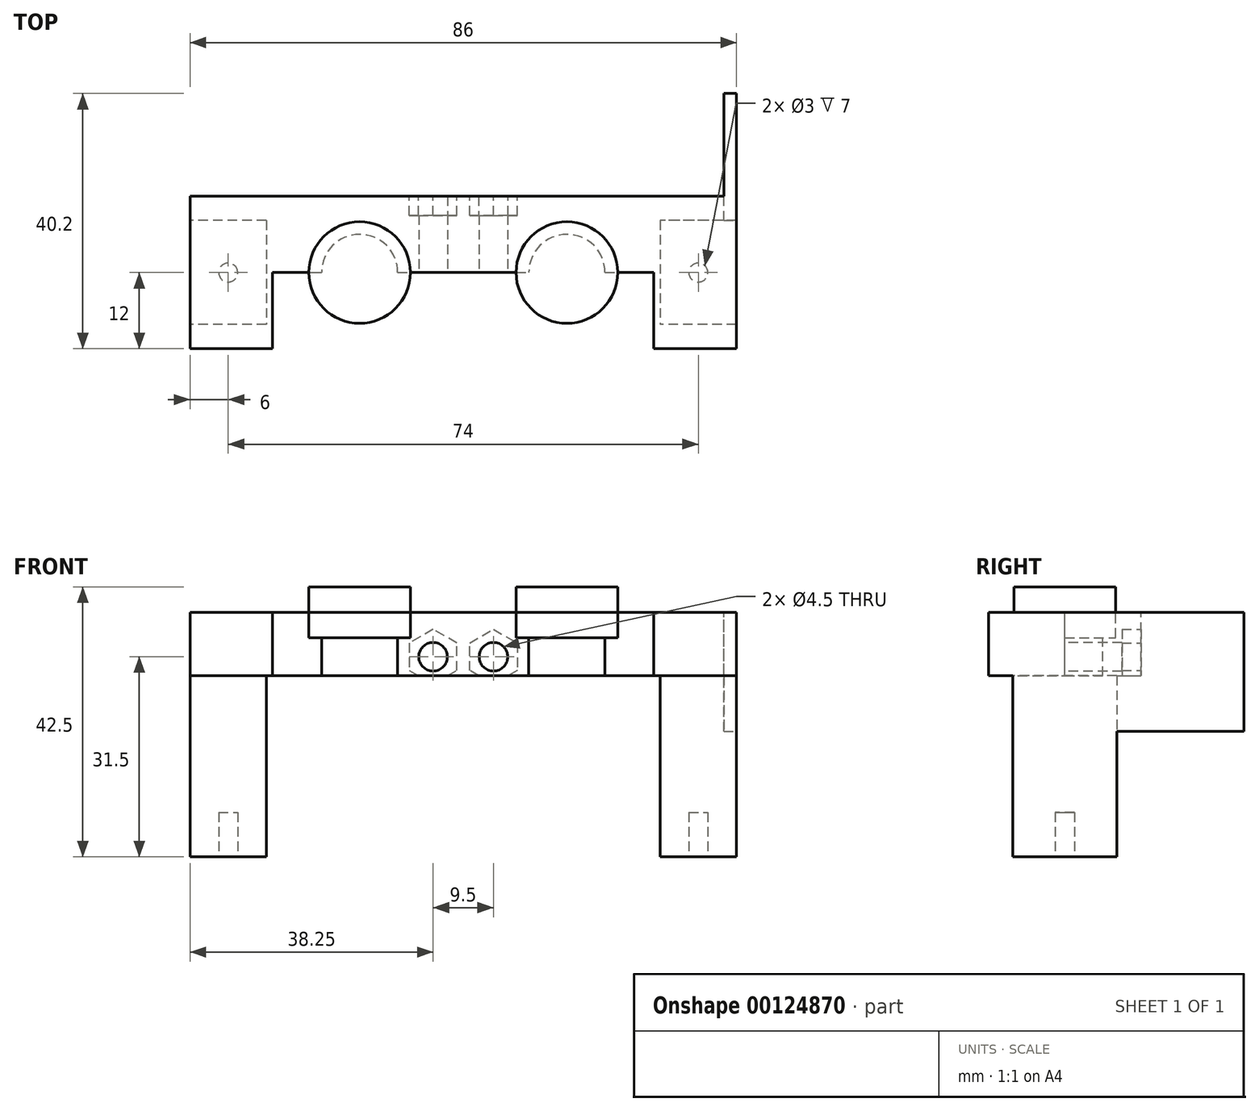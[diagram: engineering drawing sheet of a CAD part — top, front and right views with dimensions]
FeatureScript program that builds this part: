
annotation { "Feature Type Name" : "Feature", "Feature Type Description" : "" }
export const myFeature = defineFeature(function(context is Context, id is Id, definition is map)
    precondition{}
    {
        {
            var Q0;
            Q0=qCreatedBy(makeId("Top.planeOp"),FACE);
            var sketch = newSketch(context, id + "F0", { "sketchPlane" : qUnion([Q0])});
            skLineSegment(sketch, "E0.bottom", {"start": v(43, -44.5) * mm, "end": v(-43, -44.5) * mm});
            skLineSegment(sketch, "E0.top", {"start": v(43, 44.5) * mm, "end": v(-43, 44.5) * mm});
            skLineSegment(sketch, "E0.left", {"start": v(43, -44.5) * mm, "end": v(43, 44.5) * mm});
            skLineSegment(sketch, "E0.right", {"start": v(-43, -44.5) * mm, "end": v(-43, 44.5) * mm});
            skPoint(sketch, "E0.middle", {"position": v(0, 0) * mm});
            skLineSegment(sketch, "E1.bottom", {"start": v(-31, 25.5) * mm, "end": v(31, 25.5) * mm});
            skLineSegment(sketch, "E1.top", {"start": v(-31, -11.5) * mm, "end": v(31, -11.5) * mm});
            skLineSegment(sketch, "E1.left", {"start": v(-31, 25.5) * mm, "end": v(-31, -11.5) * mm});
            skLineSegment(sketch, "E1.right", {"start": v(31, 25.5) * mm, "end": v(31, -11.5) * mm});
            skLineSegment(sketch, "E2.bottom", {"start": v(43, 13.5) * mm, "end": v(31, 13.5) * mm});
            skLineSegment(sketch, "E2.top", {"start": v(43, -3) * mm, "end": v(31, -3) * mm});
            skLineSegment(sketch, "E2.left", {"start": v(43, 13.5) * mm, "end": v(43, -3) * mm});
            skLineSegment(sketch, "E2.right", {"start": v(-43, 13.5) * mm, "end": v(-43, -3) * mm});
            skLineSegment(sketch, "E3", {"start": v(-43, 5.25) * mm, "end": v(-31, 5.25) * mm, "construction": true});
            skLineSegment(sketch, "E4.trimOffspring", {"start": v(-31, 13.5) * mm, "end": v(-43, 13.5) * mm});
            skLineSegment(sketch, "E5.trimOffspring", {"start": v(-31, -3) * mm, "end": v(-43, -3) * mm});
            skLineSegment(sketch, "E6.trimOffspring", {"start": v(31, 5.25) * mm, "end": v(43, 5.25) * mm, "construction": true});
            skPoint(sketch, "E7", {"position": v(-37, 5.25) * mm});
            skPoint(sketch, "E8", {"position": v(37, 5.25) * mm});
            skCircle(sketch, "E9", {"center": v(37, 5.25) * mm, "radius": 1.6 * mm});
            skPoint(sketch, "E10", {"position": v(38.6, 5.25) * mm});
            skCircle(sketch, "E11.MirrorC", {"center": v(-37, 5.25) * mm, "radius": 1.6 * mm});
            skSolve(sketch);
        }
        {
            var Q0;
            Q0=qSketchRegion(id+"F0",true);
            extrude(context, id + "F1", {"entities" : qUnion([Q0]), "depth" : 17.5 * mm});
        }
        {
            var Q0;
            Q0=makeQuery(id+"F1.opExtrude","CAP_FACE",FACE,{"disambiguationData":[OSD([sQuery(id+"F0.wireOp",EDGE,"E0.bottom"),sQuery(id+"F0.wireOp",EDGE,"E0.top"),sQuery(id+"F0.wireOp",EDGE,"E0.left"),sQuery(id+"F0.wireOp",EDGE,"E0.right"),sQuery(id+"F0.wireOp",EDGE,"E1.bottom"),sQuery(id+"F0.wireOp",EDGE,"E1.top"),sQuery(id+"F0.wireOp",EDGE,"E1.left"),sQuery(id+"F0.wireOp",EDGE,"E1.right"),sQuery(id+"F0.wireOp",EDGE,"E2.left"),sQuery(id+"F0.wireOp",EDGE,"E2.right"),sQuery(id+"F0.wireOp",EDGE,"E9"),sQuery(id+"F0.wireOp",EDGE,"E11.MirrorC")])],"isStart":false});
            var sketch = newSketch(context, id + "F2", { "sketchPlane" : qUnion([Q0])});
            skLineSegment(sketch, "E12.bottom", {"start": v(43, -2.95) * mm, "end": v(31, -2.95) * mm});
            skLineSegment(sketch, "E12.top", {"start": v(43, 13.45) * mm, "end": v(31, 13.45) * mm});
            skLineSegment(sketch, "E12.left", {"start": v(43, -2.95) * mm, "end": v(43, 13.45) * mm});
            skLineSegment(sketch, "E12.right", {"start": v(-43, -2.95) * mm, "end": v(-43, 13.45) * mm});
            skPoint(sketch, "E13", {"position": v(37, 5.25) * mm});
            skLineSegment(sketch, "E14", {"start": v(43, 5.25) * mm, "end": v(31, 5.25) * mm, "construction": true});
            skLineSegment(sketch, "E15.0", {"start": v(31, 25.5) * mm, "end": v(31, -11.5) * mm});
            skLineSegment(sketch, "E15.1", {"start": v(-31, 25.5) * mm, "end": v(-31, -11.5) * mm});
            skLineSegment(sketch, "E16.trimOffspring", {"start": v(-31, -2.95) * mm, "end": v(-43, -2.95) * mm});
            skLineSegment(sketch, "E17.trimOffspring", {"start": v(-31, 13.45) * mm, "end": v(-43, 13.45) * mm});
            skLineSegment(sketch, "E18.trimOffspring", {"start": v(-31, 5.25) * mm, "end": v(-43, 5.25) * mm, "construction": true});
            skSolve(sketch);
        }
        {
            var Q0;
            Q0=qCreatedBy(makeId("Top.planeOp"),FACE);
            var sketch = newSketch(context, id + "F3", { "sketchPlane" : qUnion([Q0])});
            skCircle(sketch, "E19", {"center": v(16.32, 5.25) * mm, "radius": 11.2 * mm});
            skCircle(sketch, "E20.0", {"center": v(-37, 5.25) * mm, "radius": 1.6 * mm});
            skLineSegment(sketch, "E21", {"start": v(-37, 5.25) * mm, "end": v(47.23, 5.25) * mm, "construction": true});
            skCircle(sketch, "E22.MirrorC", {"center": v(-16.32, 5.25) * mm, "radius": 11.2 * mm});
            skSolve(sketch);
        }
        {
            var Q0;
            Q0=makeQuery(id+"F3.imprint","IMPRINT",FACE,{"disambiguationData":[TD([[makeQuery(id+"F3.imprint","IMPRINT",EDGE,{"derivedFrom":sQuery(id+"F3.wireOp",EDGE,"E19")}),1.0]])]});
            var Q1;
            Q1=makeQuery(id+"F3.imprint","IMPRINT",FACE,{"disambiguationData":[TD([[makeQuery(id+"F3.imprint","IMPRINT",EDGE,{"derivedFrom":sQuery(id+"F3.wireOp",EDGE,"E22.MirrorC")}),-1.0]])]});
            extrude(context, id + "F4", {"entities" : qUnion([Q0, Q1]), "depth" : (26 + 14.5) * mm, "hasSecondDirection" : true, "secondDirectionOppositeDirection" : false, "secondDirectionDepth" : 14.5 * mm});
        }
        {
            var Q0;
            Q0=makeQuery(id+"F1.opExtrude","CAP_FACE",FACE,{"disambiguationData":[OSD([sQuery(id+"F0.wireOp",EDGE,"E0.bottom"),sQuery(id+"F0.wireOp",EDGE,"E0.top"),sQuery(id+"F0.wireOp",EDGE,"E0.left"),sQuery(id+"F0.wireOp",EDGE,"E0.right"),sQuery(id+"F0.wireOp",EDGE,"E1.bottom"),sQuery(id+"F0.wireOp",EDGE,"E1.top"),sQuery(id+"F0.wireOp",EDGE,"E1.left"),sQuery(id+"F0.wireOp",EDGE,"E1.right"),sQuery(id+"F0.wireOp",EDGE,"E2.left"),sQuery(id+"F0.wireOp",EDGE,"E2.right"),sQuery(id+"F0.wireOp",EDGE,"E9"),sQuery(id+"F0.wireOp",EDGE,"E11.MirrorC")])],"isStart":false});
            var sketch = newSketch(context, id + "F5", { "sketchPlane" : qUnion([Q0])});
            skLineSegment(sketch, "E23.bottom", {"start": v(-43, 13.5) * mm, "end": v(-31, 13.5) * mm});
            skLineSegment(sketch, "E23.top", {"start": v(-43, -3) * mm, "end": v(-31, -3) * mm});
            skLineSegment(sketch, "E23.left", {"start": v(-43, 13.5) * mm, "end": v(-43, -3) * mm});
            skLineSegment(sketch, "E23.right", {"start": v(43, 13.5) * mm, "end": v(43, -3) * mm});
            skPoint(sketch, "E24", {"position": v(43, 5.25) * mm});
            skPoint(sketch, "E25", {"position": v(-43, 5.25) * mm});
            skLineSegment(sketch, "E26", {"start": v(-31, 13.5) * mm, "end": v(-31, -3) * mm});
            skLineSegment(sketch, "E27", {"start": v(31, 13.5) * mm, "end": v(31, -3) * mm});
            skLineSegment(sketch, "E28.trimOffspring", {"start": v(31, 13.5) * mm, "end": v(43, 13.5) * mm});
            skLineSegment(sketch, "E29.trimOffspring", {"start": v(31, -3) * mm, "end": v(43, -3) * mm});
            skSolve(sketch);
        }
        {
            var Q0;
            Q0=qSketchRegion(id+"F5",true);
            extrude(context, id + "F6", {"entities" : qUnion([Q0]), "operationType" : NewBodyOperationType.REMOVE, "oppositeDirection" : true, "depth" : 3 * mm});
        }
        {
            var Q0;
            Q0=qSketchRegion(id+"F2",true);
            extrude(context, id + "F7", {"entities" : qUnion([Q0]), "depth" : 35.5 * mm, "hasSecondDirection" : true, "secondDirectionOppositeDirection" : true, "secondDirectionDepth" : 3 * mm});
        }
        {
            var Q0;
            Q0=makeQuery(id+"F4.opExtrude","CAP_FACE",FACE,{"disambiguationData":[OSD([sQuery(id+"F3.wireOp",EDGE,"E19")])],"isStart":false});
            cPlane(context, id + "F8", {"entities" : qUnion([Q0]), "cplaneType" : CPlaneType.OFFSET, "offset" : 0 * mm, "width" : 150 * mm, "height" : 150 * mm});
        }
        {
            var Q0;
            Q0=qCreatedBy(id+"F8.planeOp",FACE);
            var sketch = newSketch(context, id + "F9", { "sketchPlane" : qUnion([Q0])});
            skCircle(sketch, "E30", {"center": v(16.32, 5.25) * mm, "radius": 8 * mm});
            skCircle(sketch, "E31.MirrorC", {"center": v(-16.32, 5.25) * mm, "radius": 8 * mm});
            skSolve(sketch);
        }
        {
            var Q0;
            Q0=qSketchRegion(id+"F9",true);
            extrude(context, id + "F10", {"entities" : qUnion([Q0]), "depth" : 16.5 * mm});
        }
        {
            var Q0;
            Q0=makeQuery(id+"F1.opExtrude","SWEPT_FACE",FACE,{"disambiguationData":[OSD([sQuery(id+"F0.wireOp",EDGE,"E0.right"),sQuery(id+"F0.wireOp",EDGE,"E2.right")])]});
            var sketch = newSketch(context, id + "F11", { "sketchPlane" : qUnion([Q0])});
            skLineSegment(sketch, "E32.bottom", {"start": v(-25, 0) * mm, "end": v(25, 0) * mm});
            skLineSegment(sketch, "E32.top", {"start": v(-25, 5.5) * mm, "end": v(25, 5.5) * mm});
            skLineSegment(sketch, "E32.left", {"start": v(-25, 0) * mm, "end": v(-25, 5.5) * mm});
            skLineSegment(sketch, "E32.right", {"start": v(25, 0) * mm, "end": v(25, 5.5) * mm});
            skSolve(sketch);
        }
        {
            var Q0;
            Q0=qSketchRegion(id+"F11",true);
            extrude(context, id + "F12", {"entities" : qUnion([Q0]), "operationType" : NewBodyOperationType.REMOVE, "oppositeDirection" : true, "depth" : 90 * mm});
        }
        {
            var Q0;
            Q0=makeQuery(id+"F7.opExtrude","CAP_FACE",FACE,{"disambiguationData":[OSD([sQuery(id+"F2.wireOp",EDGE,"E12.right"),sQuery(id+"F2.wireOp",EDGE,"E15.1"),sQuery(id+"F2.wireOp",EDGE,"E16.trimOffspring"),sQuery(id+"F2.wireOp",EDGE,"E17.trimOffspring")])],"isStart":false});
            var sketch = newSketch(context, id + "F13", { "sketchPlane" : qUnion([Q0])});
            skLineSegment(sketch, "E33.0", {"start": v(43, 13.5) * mm, "end": v(43, 17.25) * mm});
            skLineSegment(sketch, "E34.bottom", {"start": v(-43, -6.75) * mm, "end": v(43, -6.75) * mm});
            skLineSegment(sketch, "E34.top", {"start": v(-43, 17.25) * mm, "end": v(43, 17.25) * mm});
            skLineSegment(sketch, "E34.left", {"start": v(-43, -6.75) * mm, "end": v(-43, 17.25) * mm});
            skLineSegment(sketch, "E34.right", {"start": v(43, -6.75) * mm, "end": v(43, 17.25) * mm});
            skSolve(sketch);
        }
        {
            var Q0;
            Q0=qSketchRegion(id+"F13",true);
            extrude(context, id + "F14", {"entities" : qUnion([Q0]), "operationType" : NewBodyOperationType.ADD, "oppositeDirection" : true, "depth" : 10 * mm});
        }
        {
            var Q0;
            Q0=makeQuery(id+"F7.opExtrude","CAP_FACE",FACE,{"disambiguationData":[OSD([sQuery(id+"F2.wireOp",EDGE,"E12.bottom"),sQuery(id+"F2.wireOp",EDGE,"E12.top"),sQuery(id+"F2.wireOp",EDGE,"E12.left"),sQuery(id+"F2.wireOp",EDGE,"E15.0")])],"isStart":true});
            var sketch = newSketch(context, id + "F15", { "sketchPlane" : qUnion([Q0])});
            skCircle(sketch, "E35", {"center": v(-37, -5.25) * mm, "radius": 1.5 * mm});
            skCircle(sketch, "E36.MirrorC", {"center": v(37, -5.25) * mm, "radius": 1.5 * mm});
            skSolve(sketch);
        }
        {
            var Q0;
            Q0=qSketchRegion(id+"F15",true);
            extrude(context, id + "F16", {"entities" : qUnion([Q0]), "operationType" : NewBodyOperationType.REMOVE, "oppositeDirection" : true, "depth" : 7 * mm});
        }
        {
            var Q0;
            Q0=makeQuery(id+"F14.boolean.opBoolean","MERGE",FACE,{"derivedFrom":[makeQuery(id+"F7.opExtrude","CAP_FACE",FACE,{"disambiguationData":[OSD([sQuery(id+"F2.wireOp",EDGE,"E12.bottom"),sQuery(id+"F2.wireOp",EDGE,"E12.top"),sQuery(id+"F2.wireOp",EDGE,"E12.left"),sQuery(id+"F2.wireOp",EDGE,"E15.0")])],"isStart":false}),makeQuery(id+"F7.opExtrude","CAP_FACE",FACE,{"disambiguationData":[OSD([sQuery(id+"F2.wireOp",EDGE,"E12.right"),sQuery(id+"F2.wireOp",EDGE,"E15.1"),sQuery(id+"F2.wireOp",EDGE,"E16.trimOffspring"),sQuery(id+"F2.wireOp",EDGE,"E17.trimOffspring")])],"isStart":false}),makeQuery(id+"F14.opExtrude","CAP_FACE",FACE,{"disambiguationData":[OSD([sQuery(id+"F13.wireOp",EDGE,"E34.bottom"),sQuery(id+"F13.wireOp",EDGE,"E34.top"),sQuery(id+"F13.wireOp",EDGE,"E34.left"),sQuery(id+"F13.wireOp",EDGE,"E34.right")])],"isStart":true})]});
            var sketch = newSketch(context, id + "F17", { "sketchPlane" : qUnion([Q0])});
            skCircle(sketch, "E37.0", {"center": v(16.32, 5.25) * mm, "radius": 8 * mm});
            skCircle(sketch, "E37.1", {"center": v(-16.32, 5.25) * mm, "radius": 8 * mm});
            skSolve(sketch);
        }
        {
            var Q0;
            Q0=qSketchRegion(id+"F17",true);
            extrude(context, id + "F18", {"entities" : qUnion([Q0]), "operationType" : NewBodyOperationType.REMOVE, "oppositeDirection" : true, "depth" : 15 * mm});
        }
        {
            var Q0;
            Q0=makeQuery(id+"F1.opExtrude","SWEPT_BODY",BODY,{"disambiguationData":[OSD([sQuery(id+"F0.wireOp",EDGE,"E0.bottom"),sQuery(id+"F0.wireOp",EDGE,"E0.top"),sQuery(id+"F0.wireOp",EDGE,"E0.left"),sQuery(id+"F0.wireOp",EDGE,"E0.right"),sQuery(id+"F0.wireOp",EDGE,"E1.bottom"),sQuery(id+"F0.wireOp",EDGE,"E1.top"),sQuery(id+"F0.wireOp",EDGE,"E1.left"),sQuery(id+"F0.wireOp",EDGE,"E1.right"),sQuery(id+"F0.wireOp",EDGE,"E2.left"),sQuery(id+"F0.wireOp",EDGE,"E2.right"),sQuery(id+"F0.wireOp",EDGE,"E9"),sQuery(id+"F0.wireOp",EDGE,"E11.MirrorC")])]});
            deleteBodies(context, id + "F19", {"entities" : qUnion([Q0])});
        }
        {
            var Q0;
            Q0=makeQuery(id+"F4.opExtrude","SWEPT_BODY",BODY,{"disambiguationData":[OSD([sQuery(id+"F3.wireOp",EDGE,"E19")])]});
            var Q1;
            Q1=makeQuery(id+"F4.opExtrude","SWEPT_BODY",BODY,{"disambiguationData":[OSD([sQuery(id+"F3.wireOp",EDGE,"E22.MirrorC")])]});
            var Q2;
            Q2=makeQuery(id+"F10.opExtrude","SWEPT_BODY",BODY,{"disambiguationData":[OSD([sQuery(id+"F9.wireOp",EDGE,"E30")])]});
            var Q3;
            Q3=makeQuery(id+"F10.opExtrude","SWEPT_BODY",BODY,{"disambiguationData":[OSD([sQuery(id+"F9.wireOp",EDGE,"E31.MirrorC")])]});
            deleteBodies(context, id + "F20", {"entities" : qUnion([Q0, Q1, Q2, Q3])});
        }
        {
            var Q0;
            Q0=makeQuery(id+"F14.boolean.opBoolean","MERGE",FACE,{"derivedFrom":[makeQuery(id+"F7.opExtrude","CAP_FACE",FACE,{"disambiguationData":[OSD([sQuery(id+"F2.wireOp",EDGE,"E12.bottom"),sQuery(id+"F2.wireOp",EDGE,"E12.top"),sQuery(id+"F2.wireOp",EDGE,"E12.left"),sQuery(id+"F2.wireOp",EDGE,"E15.0")])],"isStart":false}),makeQuery(id+"F7.opExtrude","CAP_FACE",FACE,{"disambiguationData":[OSD([sQuery(id+"F2.wireOp",EDGE,"E12.right"),sQuery(id+"F2.wireOp",EDGE,"E15.1"),sQuery(id+"F2.wireOp",EDGE,"E16.trimOffspring"),sQuery(id+"F2.wireOp",EDGE,"E17.trimOffspring")])],"isStart":false}),makeQuery(id+"F14.opExtrude","CAP_FACE",FACE,{"disambiguationData":[OSD([sQuery(id+"F13.wireOp",EDGE,"E34.bottom"),sQuery(id+"F13.wireOp",EDGE,"E34.top"),sQuery(id+"F13.wireOp",EDGE,"E34.left"),sQuery(id+"F13.wireOp",EDGE,"E34.right")])],"isStart":true})]});
            cPlane(context, id + "F21", {"entities" : qUnion([Q0]), "cplaneType" : CPlaneType.OFFSET, "offset" : 4 * mm, "oppositeDirection" : true, "width" : 150 * mm, "height" : 150 * mm});
        }
        {
            var Q0;
            Q0=qCreatedBy(id+"F21.planeOp",FACE);
            var sketch = newSketch(context, id + "F22", { "sketchPlane" : qUnion([Q0])});
            skCircle(sketch, "E38.0", {"center": v(-16.32, 5.25) * mm, "radius": 8 * mm});
            skCircle(sketch, "E39", {"center": v(-16.32, 5.25) * mm, "radius": 6 * mm});
            skCircle(sketch, "E40.MirrorC", {"center": v(16.32, 5.25) * mm, "radius": 6 * mm});
            skCircle(sketch, "E41.0", {"center": v(16.32, 5.25) * mm, "radius": 8 * mm});
            skSolve(sketch);
        }
        {
            var Q0;
            Q0 = qSketchRegion(id + "F22", true);
            extrude(context, id + "F23", {"entities" : qUnion([Q0]), "operationType" : NewBodyOperationType.ADD, "oppositeDirection" : true, "depth" : 6 * mm});
        }
        {
            var Q0;
            Q0=makeQuery(id+"F14.boolean.opBoolean","MERGE",FACE,{"derivedFrom":[makeQuery(id+"F7.opExtrude","CAP_FACE",FACE,{"disambiguationData":[OSD([sQuery(id+"F2.wireOp",EDGE,"E12.bottom"),sQuery(id+"F2.wireOp",EDGE,"E12.top"),sQuery(id+"F2.wireOp",EDGE,"E12.left"),sQuery(id+"F2.wireOp",EDGE,"E15.0")])],"isStart":false}),makeQuery(id+"F7.opExtrude","CAP_FACE",FACE,{"disambiguationData":[OSD([sQuery(id+"F2.wireOp",EDGE,"E12.right"),sQuery(id+"F2.wireOp",EDGE,"E15.1"),sQuery(id+"F2.wireOp",EDGE,"E16.trimOffspring"),sQuery(id+"F2.wireOp",EDGE,"E17.trimOffspring")])],"isStart":false}),makeQuery(id+"F14.opExtrude","CAP_FACE",FACE,{"disambiguationData":[OSD([sQuery(id+"F13.wireOp",EDGE,"E34.bottom"),sQuery(id+"F13.wireOp",EDGE,"E34.top"),sQuery(id+"F13.wireOp",EDGE,"E34.left"),sQuery(id+"F13.wireOp",EDGE,"E34.right")])],"isStart":true})]});
            var sketch = newSketch(context, id + "F24", { "sketchPlane" : qUnion([Q0])});
            skLineSegment(sketch, "E42.bottom", {"start": v(-30, -6.75) * mm, "end": v(30, -6.75) * mm});
            skLineSegment(sketch, "E42.top", {"start": v(-30, 5.25) * mm, "end": v(30, 5.25) * mm});
            skLineSegment(sketch, "E42.left", {"start": v(-30, -6.75) * mm, "end": v(-30, 5.25) * mm});
            skLineSegment(sketch, "E42.right", {"start": v(30, -6.75) * mm, "end": v(30, 5.25) * mm});
            skCircle(sketch, "E43.0", {"center": v(-16.32, 5.25) * mm, "radius": 6 * mm});
            skSolve(sketch);
        }
        {
            var Q0;
            Q0 = qSketchRegion(id + "F24", true);
            extrude(context, id + "F25", {"entities" : qUnion([Q0]), "operationType" : NewBodyOperationType.REMOVE, "oppositeDirection" : true, "depth" : 25 * mm});
        }
        {
            var Q0;
            {var subQ5=sQuery(id+"F17.wireOp",EDGE,"E37.0");var subQ8=sQuery(id+"F17.wireOp",EDGE,"E37.1");var subQ10=sQuery(id+"F24.wireOp",EDGE,"E42.top");var subQ11=makeQuery(id+"F18.boolean.opBoolean","COPY",EDGE,{"derivedFrom":makeQuery(id+"F18.opExtrude","CAP_EDGE",EDGE,{"disambiguationData":[OSD([subQ5])],"isStart":true})});var subQ13=makeQuery(id+"F24.imprint","INTERSECT",VERTEX,{"disambiguationData":[OD(0.0)],"derivedFrom":[subQ11,subQ10]});var subQ14=makeQuery(id+"F24.imprint","INTERSECT",VERTEX,{"disambiguationData":[OD(1.0)],"derivedFrom":[makeQuery(id+"F18.boolean.opBoolean","COPY",EDGE,{"derivedFrom":makeQuery(id+"F18.opExtrude","CAP_EDGE",EDGE,{"disambiguationData":[OSD([subQ8])],"isStart":true})}),subQ10]});Q0=makeQuery(id+"F25.boolean.opBoolean","COPY",FACE,{"disambiguationData":[TD([makeQuery(id+"F18.boolean.opBoolean","COPY",FACE,{"derivedFrom":makeQuery(id+"F18.opExtrude","SWEPT_FACE",FACE,{"disambiguationData":[OSD([subQ8])]})})])],"derivedFrom":makeQuery(id+"F25.opExtrude","SWEPT_FACE",FACE,{"disambiguationData":[OSD([subQ10]),TDD([makeQuery(id+"F24.imprint","IMPRINT",EDGE,{"disambiguationData":[TD([[makeQuery(id+"F24.imprint","INTERSECT",VERTEX,{"disambiguationData":[OD(1.0)],"derivedFrom":[subQ10,sQuery(id+"F24.wireOp",EDGE,"E43.0")]}),-1.0]])],"derivedFrom":subQ10}),makeQuery(id+"F24.imprint","IMPRINT",EDGE,{"disambiguationData":[TD([[subQ14,-1.0]])],"derivedFrom":subQ10}),makeQuery(id+"F24.imprint","IMPRINT",EDGE,{"disambiguationData":[TD([[subQ13,-1.0]])],"derivedFrom":subQ10}),makeQuery(id+"F24.imprint","IMPRINT",EDGE,{"disambiguationData":[TD([[makeQuery(id+"F24.imprint","INTERSECT",VERTEX,{"derivedFrom":[subQ10,sQuery(id+"F24.wireOp",EDGE,"E42.right")]}),1.0]])],"derivedFrom":subQ10})])]})});}
            var sketch = newSketch(context, id + "F26", { "sketchPlane" : qUnion([Q0])});
            skLineSegment(sketch, "E44.0", {"start": v(-10.32, 43) * mm, "end": v(-10.32, 49) * mm});
            skLineSegment(sketch, "E45", {"start": v(-10.32, 46) * mm, "end": v(10.32, 46) * mm, "construction": true});
            skPoint(sketch, "E46", {"position": v(-4.75, 46) * mm});
            skCircle(sketch, "E47", {"center": v(-4.75, 46) * mm, "radius": 2.25 * mm});
            skCircle(sketch, "E48.MirrorC", {"center": v(4.75, 46) * mm, "radius": 2.25 * mm});
            skSolve(sketch);
        }
        {
            var Q0;
            Q0 = qSketchRegion(id + "F26", true);
            extrude(context, id + "F27", {"entities" : qUnion([Q0]), "operationType" : NewBodyOperationType.REMOVE, "oppositeDirection" : true, "depth" : 25 * mm});
        }
        {
            var Q0;
            Q0=makeQuery(id+"F14.opExtrude","SWEPT_FACE",FACE,{"disambiguationData":[OSD([sQuery(id+"F13.wireOp",EDGE,"E34.top")])]});
            var sketch = newSketch(context, id + "F28", { "sketchPlane" : qUnion([Q0])});
            skCircle(sketch, "E49.0", {"center": v(4.75, 46) * mm, "radius": 2.25 * mm});
            skCircle(sketch, "E50.cCircle", {"center": v(4.75, 46) * mm, "radius": 3.75 * mm, "construction": true});
            skLineSegment(sketch, "E50.0", {"start": v(8.5, 48.17) * mm, "end": v(8.5, 43.83) * mm});
            skLineSegment(sketch, "E50.1", {"start": v(8.5, 43.83) * mm, "end": v(4.75, 41.67) * mm});
            skLineSegment(sketch, "E50.2", {"start": v(4.75, 41.67) * mm, "end": v(1, 43.83) * mm});
            skLineSegment(sketch, "E50.3", {"start": v(1, 43.83) * mm, "end": v(1, 48.17) * mm});
            skLineSegment(sketch, "E50.4", {"start": v(1, 48.17) * mm, "end": v(4.75, 50.33) * mm});
            skLineSegment(sketch, "E50.5", {"start": v(4.75, 50.33) * mm, "end": v(8.5, 48.17) * mm});
            skPoint(sketch, "E50.0.midPoint", {"position": v(8.5, 46) * mm});
            skLineSegment(sketch, "E51.MirrorCS", {"start": v(-1, 48.17) * mm, "end": v(-4.75, 50.33) * mm});
            skLineSegment(sketch, "E52.MirrorCS", {"start": v(-1, 43.83) * mm, "end": v(-1, 48.17) * mm});
            skLineSegment(sketch, "E53.MirrorCS", {"start": v(-4.75, 41.67) * mm, "end": v(-1, 43.83) * mm});
            skLineSegment(sketch, "E54.MirrorCS", {"start": v(-8.5, 43.83) * mm, "end": v(-4.75, 41.67) * mm});
            skLineSegment(sketch, "E55.MirrorCS", {"start": v(-8.5, 48.17) * mm, "end": v(-8.5, 43.83) * mm});
            skLineSegment(sketch, "E56.MirrorCS", {"start": v(-4.75, 50.33) * mm, "end": v(-8.5, 48.17) * mm});
            skCircle(sketch, "E57.0", {"center": v(-4.75, 46) * mm, "radius": 2.25 * mm});
            skSolve(sketch);
        }
        {
            var Q0;
            Q0 = qSketchRegion(id + "F28", true);
            extrude(context, id + "F29", {"entities" : qUnion([Q0]), "operationType" : NewBodyOperationType.REMOVE, "oppositeDirection" : true, "depth" : 3 * mm});
        }
        {
            var Q0;
            Q0=makeQuery(id+"F14.boolean.opBoolean","MERGE",FACE,{"derivedFrom":[makeQuery(id+"F7.opExtrude","SWEPT_FACE",FACE,{"disambiguationData":[OSD([sQuery(id+"F2.wireOp",EDGE,"E12.left")])]}),makeQuery(id+"F14.opExtrude","SWEPT_FACE",FACE,{"disambiguationData":[OSD([sQuery(id+"F13.wireOp",EDGE,"E34.right")])]})]});
            var sketch = newSketch(context, id + "F30", { "sketchPlane" : qUnion([Q0])});
            skLineSegment(sketch, "E58.bottom", {"start": v(13.45, 34.24) * mm, "end": v(33.45, 34.24) * mm});
            skLineSegment(sketch, "E58.top", {"start": v(13.45, 53) * mm, "end": v(33.45, 53) * mm});
            skLineSegment(sketch, "E58.left", {"start": v(13.45, 34.24) * mm, "end": v(13.45, 53) * mm});
            skLineSegment(sketch, "E58.right", {"start": v(33.45, 34.24) * mm, "end": v(33.45, 53) * mm});
            skSolve(sketch);
        }
        {
            var Q0;
            Q0 = qSketchRegion(id + "F30", true);
            extrude(context, id + "F31", {"entities" : qUnion([Q0]), "operationType" : NewBodyOperationType.ADD, "oppositeDirection" : true, "depth" : 2 * mm});
        }
    });
